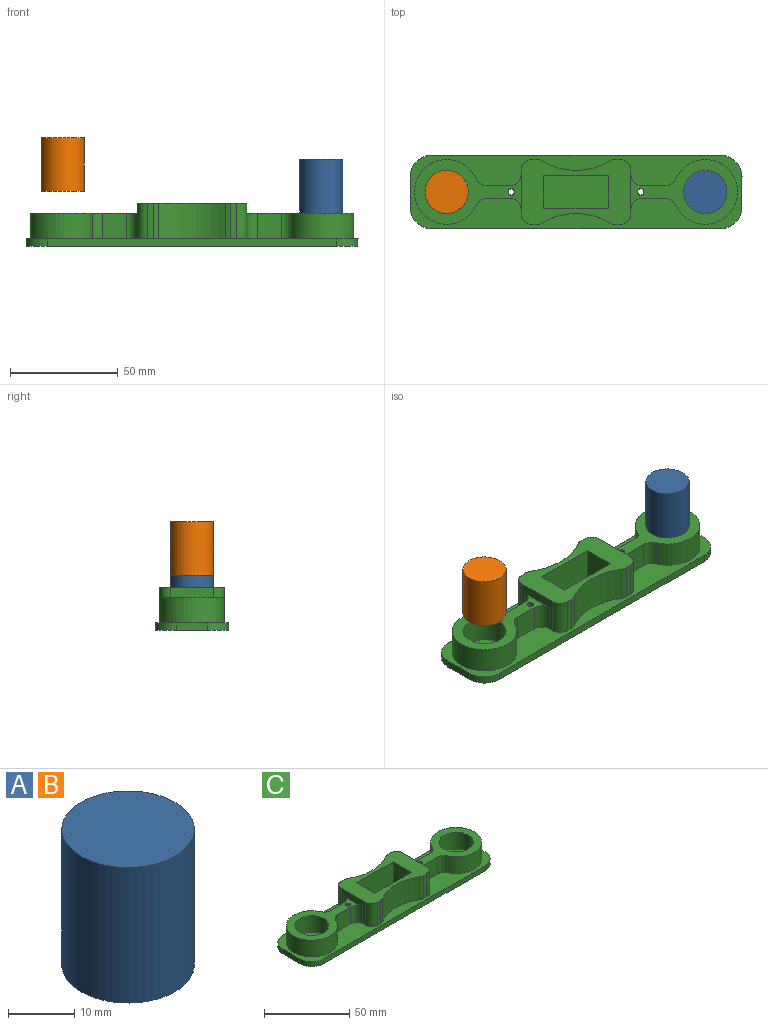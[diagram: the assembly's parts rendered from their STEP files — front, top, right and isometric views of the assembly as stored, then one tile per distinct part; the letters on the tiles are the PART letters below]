
ASSEMBLY  parts=3 mates=2
PART A: 3 faces, bbox 20x20x25 mm
  f0: cylinder r=10mm len=25mm, axis (0,0,-1), area 1570.8mm2, adj f1,f2
  f1: plane 20x20mm, normal (0,0,1), area 314.2mm2, adj f0
  f2: plane 20x20mm, normal (0,0,-1), area 314.2mm2, adj f0
PART B: same geometry as A
PART C: 56 faces, bbox 154x34x20 mm
  f0: plane 154x34mm, normal (0,0,1), area 2187.4mm2, adj f1,f2,f3,f4,f5,f6,f7,f8
  f1: plane 14x3.5mm, normal (-1,0,0), area 49mm2, adj f0,f2,f8,f9
  f2: cylinder r=10mm len=10mm, axis (0,0,1), area 55mm2, adj f0,f1,f3,f9
  f3: plane 134x3.5mm, normal (0,-1,0), area 469mm2, adj f0,f2,f4,f9
  f4: cylinder r=10mm len=10mm, axis (0,0,1), area 55mm2, adj f0,f3,f5,f9
  f5: plane 14x3.5mm, normal (1,0,0), area 49mm2, adj f0,f4,f6,f9
  f6: cylinder r=10mm len=10mm, axis (0,0,1), area 55mm2, adj f0,f5,f7,f9
  f7: plane 134x3.5mm, normal (0,1,0), area 469mm2, adj f0,f6,f8,f9
  f8: cylinder r=10mm len=10mm, axis (0,0,1), area 55mm2, adj f0,f1,f7,f9
  f9: plane 154x34mm, normal (0,0,-1), area 5110.9mm2, adj f1,f2,f3,f4,f5,f6,f7,f8
  f10: plane 30x16.5mm, normal (0,-1,0), area 495mm2, adj f11,f43,f44,f45
  f11: plane 16.5x15mm, normal (-1,0,0), area 247.5mm2, adj f10,f12,f44,f45
  f12: plane 30x16.5mm, normal (0,1,0), area 495mm2, adj f11,f43,f44,f45
  f13: cylinder r=5mm len=12mm, axis (0,0,-1), area 94.2mm2, adj f0,f14,f20,f47
  f14: plane 12x11.17mm, normal (0,1,0), area 134mm2, adj f0,f13,f15,f47
  f15: cylinder r=5mm len=12mm, axis (0,0,-1), area 69.6mm2, adj f0,f14,f16,f47
  f16: cylinder r=15mm len=30mm, axis (0,0,-1), area 980.3mm2, adj f0,f15,f17,f47
  f17: cylinder r=5.44mm len=12mm, axis (0,0,-1), area 74.8mm2, adj f0,f16,f18,f47
  f18: plane 12x10.88mm, normal (0,-1,0), area 130.6mm2, adj f0,f17,f19,f47
  f19: cylinder r=5mm len=12mm, axis (0,0,-1), area 94.2mm2, adj f0,f18,f20,f47
  f20: plane 20x16.5mm, normal (-1,0,0), area 138mm2, adj f0,f13,f19,f21,f42,f44,f47
  f21: cylinder r=5mm len=16.5mm, axis (0,0,-1), area 129.6mm2, adj f0,f20,f22,f44
  f22: plane 16.5x2.47mm, normal (0,-1,0), area 40.8mm2, adj f0,f21,f23,f44
  f23: cylinder r=5mm len=16.5mm, axis (0,0,-1), area 44.6mm2, adj f0,f22,f24,f44
  f24: cylinder r=30mm len=30.9mm, axis (0,0,-1), area 535.7mm2, adj f0,f23,f25,f44
  f25: cylinder r=5mm len=16.5mm, axis (0,0,-1), area 44.6mm2, adj f0,f24,f26,f44
  f26: plane 16.5x2.47mm, normal (0,-1,0), area 40.8mm2, adj f0,f25,f27,f44
  f27: cylinder r=5mm len=16.5mm, axis (0,0,-1), area 129.6mm2, adj f0,f26,f28,f44
  f28: plane 20x16.5mm, normal (1,0,0), area 138mm2, adj f0,f27,f29,f35,f36,f44,f46
  f29: cylinder r=5mm len=12mm, axis (0,0,-1), area 94.2mm2, adj f0,f28,f30,f46
  f30: plane 12x10.88mm, normal (0,-1,0), area 130.6mm2, adj f0,f29,f31,f46
  f31: cylinder r=5.44mm len=12mm, axis (0,0,-1), area 74.8mm2, adj f0,f30,f32,f46
  f32: cylinder r=15mm len=30mm, axis (0,0,-1), area 980.3mm2, adj f0,f31,f33,f46
  f33: cylinder r=5mm len=12mm, axis (0,0,-1), area 69.6mm2, adj f0,f32,f34,f46
  f34: plane 12x11.17mm, normal (0,1,0), area 134mm2, adj f0,f33,f35,f46
  f35: cylinder r=5mm len=12mm, axis (0,0,-1), area 94.2mm2, adj f0,f28,f34,f46
  f36: cylinder r=5mm len=16.5mm, axis (0,0,-1), area 129.6mm2, adj f0,f28,f37,f44
  f37: plane 16.5x2.47mm, normal (0,1,0), area 40.8mm2, adj f0,f36,f38,f44
  f38: cylinder r=5mm len=16.5mm, axis (0,0,-1), area 44.6mm2, adj f0,f37,f39,f44
  f39: cylinder r=30mm len=30.9mm, axis (0,0,-1), area 535.7mm2, adj f0,f38,f40,f44
  f40: cylinder r=5mm len=16.5mm, axis (0,0,-1), area 44.6mm2, adj f0,f39,f41,f44
  f41: plane 16.5x2.47mm, normal (0,1,0), area 40.8mm2, adj f0,f40,f42,f44
  f42: cylinder r=5mm len=16.5mm, axis (0,0,-1), area 129.6mm2, adj f0,f20,f41,f44
  f43: plane 16.5x15mm, normal (1,0,0), area 247.5mm2, adj f10,f12,f44,f45
  f44: plane 51x30mm, normal (0,0,1), area 832.7mm2, adj f10,f11,f12,f20,f21,f22,f23,f24
  f45: plane 30x15mm, normal (0,0,1), area 450mm2, adj f10,f11,f12,f43
  f46: plane 49.5x30mm, normal (0,0,1), area 518.8mm2, adj f28,f29,f30,f31,f32,f33,f34,f35
  f47: plane 49.5x30mm, normal (0,0,1), area 518.8mm2, adj f13,f14,f15,f16,f17,f18,f19,f20
  f48: plane 20x20mm, normal (0,0,1), area 314.2mm2, adj f49
  f49: cylinder r=10mm len=20mm, axis (0,0,-1), area 754mm2, adj f47,f48
  f50: plane 20x20mm, normal (0,0,1), area 314.2mm2, adj f51
  f51: cylinder r=10mm len=20mm, axis (0,0,-1), area 754mm2, adj f46,f50
  f52: cylinder r=1.5mm len=14.5mm, axis (0,0,1), area 136.7mm2, adj f47,f54
  f53: cylinder r=1.5mm len=14.5mm, axis (0,0,1), area 136.7mm2, adj f46,f55
  f54: cone r=1.5mm half-angle=45deg, axis (0,0,-1), area 17.8mm2, adj f9,f52
  f55: cone r=1.5mm half-angle=45deg, axis (0,0,-1), area 17.8mm2, adj f9,f53
PLACE A t=(181.73,13.81,-16.02)mm
PLACE B t=(61.73,13.81,-6.02)mm
PLACE C t=(1.07,8.39,-28.02)mm
MATE slider B.f0 <-> C.f16  axis (0,0,-1) through (18.07,25.39,-6.02)mm
MATE fastened A.f0 <-> C.f32  axis (0,0,-1) through (138.07,25.39,-16.02)mm
